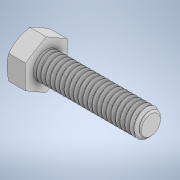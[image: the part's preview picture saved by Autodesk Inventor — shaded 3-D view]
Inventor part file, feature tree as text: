
AUTODESK INVENTOR PART (.ipt)
format: ipt  version: 2021 (Build 250183000, 183)  size: 612,864 bytes
history: native  units: in
note: dims shown in document units (in); Inventor stores cm internally (conversion verified against a paired STEP export)
features: revolve x1
ambient origin geometry x8: Origin, YZ Plane, XZ Plane, XY Plane, X Axis, Y Axis, Z Axis, Center Point
bodies: Solid1 (feature_tree)
feature tree (1):
  revolve  "Revolve7"  [1 undecoded]
note: 1 required parameter value undecoded (feature->parameter linkage not recoverable at this tier; creation-order binding heuristic only, values carry confidence <= 0.55)
